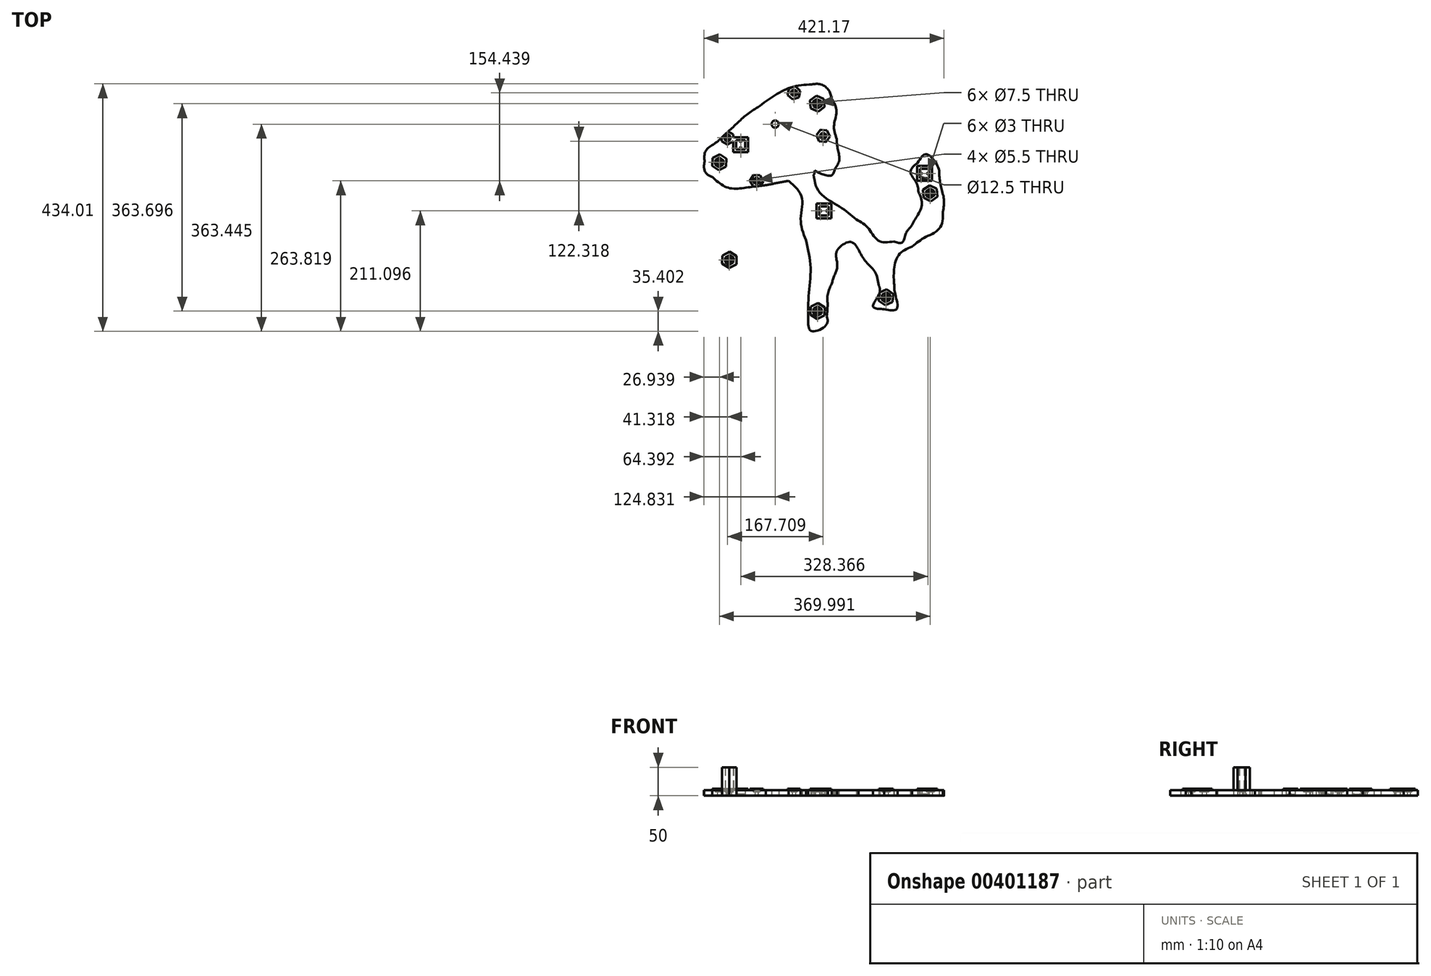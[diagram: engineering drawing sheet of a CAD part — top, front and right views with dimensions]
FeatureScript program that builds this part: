
annotation { "Feature Type Name" : "Feature", "Feature Type Description" : "" }
export const myFeature = defineFeature(function(context is Context, id is Id, definition is map)
    precondition{}
    {
        {
            var Q0;
            Q0=qCreatedBy(makeId("Top.planeOp"),FACE);
            var sketch = newSketch(context, id + "F0", { "sketchPlane" : qUnion([Q0])});
            skFitSpline(sketch, "E0", {"points": [v(-38.84, 161.13) * mm, v(-39.72, 129.92) * mm, v(-16.07, 104.3) * mm, v(-15.19, 73.39) * mm]});
            skFitSpline(sketch, "E1", {"points": [v(-15.19, 73.39) * mm, v(-15.53, 64.76) * mm, v(-18.42, 52.35) * mm, v(-28.63, 51.32) * mm]});
            skFitSpline(sketch, "E2", {"points": [v(-28.63, 51.32) * mm, v(-52.74, 44.98) * mm, v(-77.2, 39.98) * mm, v(-101.67, 35.25) * mm]});
            skFitSpline(sketch, "E3", {"points": [v(-101.67, 35.25) * mm, v(-133.26, 31.3) * mm, v(-168.43, 30.9) * mm, v(-195.67, 49.82) * mm]});
            skFitSpline(sketch, "E4", {"points": [v(-195.67, 49.82) * mm, v(-205.2, 54.88) * mm, v(-210.11, 65.3) * mm, v(-209.1, 75.9) * mm]});
            skFitSpline(sketch, "E5", {"points": [v(-209.1, 75.9) * mm, v(-207.12, 95.75) * mm, v(-190.25, 109.16) * mm, v(-176.41, 121.6) * mm]});
            skFitSpline(sketch, "E6", {"points": [v(-176.41, 121.6) * mm, v(-156.98, 139.28) * mm, v(-137.5, 157.08) * mm, v(-115.79, 172) * mm]});
            skFitSpline(sketch, "E7", {"points": [v(-115.79, 172) * mm, v(-87.6, 191.72) * mm, v(-55.7, 207.5) * mm, v(-21.28, 211.98) * mm]});
            skFitSpline(sketch, "E8", {"points": [v(-21.28, 211.98) * mm, v(-6.12, 212.25) * mm, v(8.26, 202.46) * mm, v(13.2, 188.07) * mm]});
            skFitSpline(sketch, "E9", {"points": [v(13.2, 188.07) * mm, v(22.3, 165.18) * mm, v(17.8, 140.05) * mm, v(22.57, 116.36) * mm]});
            skFitSpline(sketch, "E10", {"points": [v(22.57, 116.36) * mm, v(24.31, 98.94) * mm, v(27.2, 79.88) * mm, v(19.1, 63.6) * mm]});
            skFitSpline(sketch, "E11", {"points": [v(19.1, 63.6) * mm, v(13.05, 52.18) * mm, v(-8.03, 56.68) * mm, v(-17.41, 61.85) * mm]});
            skFitSpline(sketch, "E12", {"points": [v(-62.27, 43.42) * mm, v(-38.7, 13.78) * mm, v(-40.53, -25.96) * mm, v(-31.57, -60.94) * mm]});
            skFitSpline(sketch, "E13", {"points": [v(-31.57, -60.94) * mm, v(-23.4, -107.85) * mm, v(-26.4, -155.64) * mm, v(-27.47, -202.97) * mm]});
            skFitSpline(sketch, "E14", {"points": [v(-27.47, -202.97) * mm, v(-21.7, -220.56) * mm, v(4.44, -209.57) * mm, v(4.98, -194.23) * mm]});
            skFitSpline(sketch, "E15", {"points": [v(4.98, -194.23) * mm, v(6.6, -175.33) * mm, v(6.88, -156) * mm, v(13.8, -138) * mm]});
            skFitSpline(sketch, "E16", {"points": [v(13.8, -138) * mm, v(18.17, -124.09) * mm, v(23.35, -109.87) * mm, v(22.36, -95.12) * mm]});
            skFitSpline(sketch, "E17", {"points": [v(22.36, -95.12) * mm, v(24.1, -78.11) * mm, v(46.94, -64.43) * mm, v(60.72, -77.63) * mm]});
            skFitSpline(sketch, "E18", {"points": [v(60.72, -77.63) * mm, v(73.1, -98.24) * mm, v(89.77, -117.1) * mm, v(96.44, -140.58) * mm]});
            skFitSpline(sketch, "E19", {"points": [v(96.44, -140.58) * mm, v(97.66, -154.1) * mm, v(86.5, -177.33) * mm, v(105.7, -182.18) * mm]});
            skFitSpline(sketch, "E20", {"points": [v(105.7, -182.18) * mm, v(127.95, -181.8) * mm, v(125.17, -155.57) * mm, v(123.38, -140.16) * mm]});
            skFitSpline(sketch, "E21", {"points": [v(123.38, -140.16) * mm, v(123.03, -114.52) * mm, v(132.05, -86.5) * mm, v(155.03, -72.56) * mm]});
            skFitSpline(sketch, "E22", {"points": [v(155.03, -72.56) * mm, v(176.86, -56.73) * mm, v(203.36, -40.1) * mm, v(208.8, -11.55) * mm]});
            skFitSpline(sketch, "E23", {"points": [v(208.8, -11.55) * mm, v(210.76, 9.7) * mm, v(205.9, 30.86) * mm, v(202.52, 51.71) * mm]});
            skFitSpline(sketch, "E24", {"points": [v(202.52, 51.71) * mm, v(200.1, 68.08) * mm, v(179.66, 89.32) * mm, v(164.14, 73.98) * mm]});
            skFitSpline(sketch, "E25", {"points": [v(164.14, 73.98) * mm, v(151.98, 58.6) * mm, v(162.31, 39.48) * mm, v(166.07, 23) * mm]});
            skFitSpline(sketch, "E26", {"points": [v(166.07, 23) * mm, v(172.1, 1.47) * mm, v(162.48, -20.58) * mm, v(151.87, -39) * mm]});
            skFitSpline(sketch, "E27", {"points": [v(151.87, -39) * mm, v(144.15, -48.83) * mm, v(137.7, -65.26) * mm, v(122.78, -63.45) * mm]});
            skFitSpline(sketch, "E28", {"points": [v(122.78, -63.45) * mm, v(95.86, -62.15) * mm, v(77.57, -39.7) * mm, v(57.01, -25.17) * mm]});
            skFitSpline(sketch, "E29", {"points": [v(57.01, -25.17) * mm, v(28.57, -3) * mm, v(-8.3, 23.74) * mm, v(-18.27, 59.99) * mm]});
            skCircle(sketch, "E30", {"center": v(-85.42, 142.37) * mm, "radius": 6.25 * mm});
            skLineSegment(sketch, "E31", {"start": v(13.2, 188.07) * mm, "end": v(-41.55, 177.08) * mm});
            skLineSegment(sketch, "E32", {"start": v(-41.55, 177.08) * mm, "end": v(-38.84, 161.13) * mm});
            skLineSegment(sketch, "E33.bottom", {"start": v(-137.86, 98.34) * mm, "end": v(-153.86, 98.34) * mm});
            skLineSegment(sketch, "E33.top", {"start": v(-137.86, 114.34) * mm, "end": v(-153.86, 114.34) * mm});
            skLineSegment(sketch, "E33.left", {"start": v(-137.86, 98.34) * mm, "end": v(-137.86, 114.34) * mm});
            skLineSegment(sketch, "E33.right", {"start": v(-153.86, 98.34) * mm, "end": v(-153.86, 114.34) * mm});
            skPoint(sketch, "E33.middle", {"position": v(-145.86, 106.34) * mm});
            skLineSegment(sketch, "E34.bottom", {"start": v(8, -17.97) * mm, "end": v(-8, -17.97) * mm});
            skLineSegment(sketch, "E34.top", {"start": v(8, -1.97) * mm, "end": v(-8, -1.97) * mm});
            skLineSegment(sketch, "E34.left", {"start": v(8, -17.97) * mm, "end": v(8, -1.97) * mm});
            skLineSegment(sketch, "E34.right", {"start": v(-8, -17.97) * mm, "end": v(-8, -1.97) * mm});
            skPoint(sketch, "E34.middle", {"position": v(0, -9.97) * mm});
            skLineSegment(sketch, "E35.bottom", {"start": v(184.5, 47.75) * mm, "end": v(168.5, 47.75) * mm});
            skLineSegment(sketch, "E35.top", {"start": v(184.5, 63.75) * mm, "end": v(168.5, 63.75) * mm});
            skLineSegment(sketch, "E35.left", {"start": v(184.5, 47.75) * mm, "end": v(184.5, 63.75) * mm});
            skLineSegment(sketch, "E35.right", {"start": v(168.5, 47.75) * mm, "end": v(168.5, 63.75) * mm});
            skPoint(sketch, "E35.middle", {"position": v(176.5, 55.75) * mm});
            skLineSegment(sketch, "E36", {"start": v(0, 0) * mm, "end": v(0, 42.83) * mm, "construction": true});
            skLineSegment(sketch, "E37", {"start": v(-8, -1.97) * mm, "end": v(8, -17.97) * mm, "construction": true});
            skLineSegment(sketch, "E38", {"start": v(-294.78, 191.16) * mm, "end": v(0, -244.68) * mm, "construction": true});
            skLineSegment(sketch, "E39", {"start": v(279.03, -55.96) * mm, "end": v(24.58, 320.25) * mm, "construction": true});
            skLineSegment(sketch, "E40", {"start": v(285.1, -64.94) * mm, "end": v(20.46, -243.94) * mm, "construction": true});
            skLineSegment(sketch, "E41", {"start": v(92.7, 313.06) * mm, "end": v(-291.27, 53.36) * mm, "construction": true});
            skLineSegment(sketch, "E42", {"start": v(-168.93, 118.33) * mm, "end": v(-52.34, 197.19) * mm, "construction": true});
            skLineSegment(sketch, "E43", {"start": v(-52.34, 197.19) * mm, "end": v(-1.22, 121.6) * mm, "construction": true});
            skLineSegment(sketch, "E44", {"start": v(-1.22, 121.6) * mm, "end": v(-117.81, 42.75) * mm, "construction": true});
            skLineSegment(sketch, "E45", {"start": v(-117.81, 42.75) * mm, "end": v(-168.93, 118.33) * mm, "construction": true});
            skCircle(sketch, "E46", {"center": v(-117.81, 42.75) * mm, "radius": 2.75 * mm});
            skCircle(sketch, "E47.cCircle", {"center": v(-117.81, 42.75) * mm, "radius": 5.13 * mm, "construction": true});
            skLineSegment(sketch, "E47.0", {"start": v(-111.9, 42.69) * mm, "end": v(-114.9, 37.6) * mm});
            skLineSegment(sketch, "E47.1", {"start": v(-114.9, 37.6) * mm, "end": v(-120.82, 37.66) * mm});
            skLineSegment(sketch, "E47.2", {"start": v(-120.82, 37.66) * mm, "end": v(-123.73, 42.81) * mm});
            skLineSegment(sketch, "E47.3", {"start": v(-123.73, 42.81) * mm, "end": v(-120.71, 47.9) * mm});
            skLineSegment(sketch, "E47.4", {"start": v(-120.71, 47.9) * mm, "end": v(-114.8, 47.84) * mm});
            skLineSegment(sketch, "E47.5", {"start": v(-114.8, 47.84) * mm, "end": v(-111.9, 42.69) * mm});
            skPoint(sketch, "E47.0.midPoint", {"position": v(-113.4, 40.14) * mm});
            skCircle(sketch, "E48.cCircle", {"center": v(-117.81, 42.75) * mm, "radius": 10.12 * mm, "construction": true});
            skLineSegment(sketch, "E48.0", {"start": v(-106.12, 42.62) * mm, "end": v(-112.07, 32.56) * mm});
            skLineSegment(sketch, "E48.1", {"start": v(-112.07, 32.56) * mm, "end": v(-123.76, 32.69) * mm});
            skLineSegment(sketch, "E48.2", {"start": v(-123.76, 32.69) * mm, "end": v(-129.5, 42.87) * mm});
            skLineSegment(sketch, "E48.3", {"start": v(-129.5, 42.87) * mm, "end": v(-123.55, 52.94) * mm});
            skLineSegment(sketch, "E48.4", {"start": v(-123.55, 52.94) * mm, "end": v(-111.86, 52.81) * mm});
            skLineSegment(sketch, "E48.5", {"start": v(-111.86, 52.81) * mm, "end": v(-106.12, 42.62) * mm});
            skPoint(sketch, "E48.0.midPoint", {"position": v(-109.1, 37.6) * mm});
            skCircle(sketch, "E49", {"center": v(-168.93, 118.33) * mm, "radius": 2.75 * mm});
            skCircle(sketch, "E50.cCircle", {"center": v(-168.93, 118.33) * mm, "radius": 5.13 * mm, "construction": true});
            skLineSegment(sketch, "E50.0", {"start": v(-168.93, 112.42) * mm, "end": v(-174.06, 115.37) * mm});
            skLineSegment(sketch, "E50.1", {"start": v(-174.06, 115.37) * mm, "end": v(-174.06, 121.3) * mm});
            skLineSegment(sketch, "E50.2", {"start": v(-174.06, 121.3) * mm, "end": v(-168.93, 124.25) * mm});
            skLineSegment(sketch, "E50.3", {"start": v(-168.93, 124.25) * mm, "end": v(-163.8, 121.3) * mm});
            skLineSegment(sketch, "E50.4", {"start": v(-163.8, 121.3) * mm, "end": v(-163.8, 115.37) * mm});
            skLineSegment(sketch, "E50.5", {"start": v(-163.8, 115.37) * mm, "end": v(-168.93, 112.42) * mm});
            skPoint(sketch, "E50.0.midPoint", {"position": v(-171.5, 113.9) * mm});
            skCircle(sketch, "E51.cCircle", {"center": v(-168.93, 118.33) * mm, "radius": 10.12 * mm, "construction": true});
            skLineSegment(sketch, "E51.0", {"start": v(-158.8, 112.49) * mm, "end": v(-168.93, 106.64) * mm});
            skLineSegment(sketch, "E51.1", {"start": v(-168.93, 106.64) * mm, "end": v(-179.06, 112.49) * mm});
            skLineSegment(sketch, "E51.2", {"start": v(-179.06, 112.49) * mm, "end": v(-179.06, 124.18) * mm});
            skLineSegment(sketch, "E51.3", {"start": v(-179.06, 124.18) * mm, "end": v(-168.93, 130.03) * mm});
            skLineSegment(sketch, "E51.4", {"start": v(-168.93, 130.03) * mm, "end": v(-158.8, 124.18) * mm});
            skLineSegment(sketch, "E51.5", {"start": v(-158.8, 124.18) * mm, "end": v(-158.8, 112.49) * mm});
            skPoint(sketch, "E51.0.midPoint", {"position": v(-163.87, 109.57) * mm});
            skLineSegment(sketch, "E52.bottom", {"start": v(-132.86, 93.34) * mm, "end": v(-158.86, 93.34) * mm});
            skLineSegment(sketch, "E52.top", {"start": v(-132.86, 119.34) * mm, "end": v(-158.86, 119.34) * mm});
            skLineSegment(sketch, "E52.left", {"start": v(-132.86, 93.34) * mm, "end": v(-132.86, 119.34) * mm});
            skLineSegment(sketch, "E52.right", {"start": v(-158.86, 93.34) * mm, "end": v(-158.86, 119.34) * mm});
            skLineSegment(sketch, "E53.bottom", {"start": v(13, -22.97) * mm, "end": v(-13, -22.97) * mm});
            skLineSegment(sketch, "E53.top", {"start": v(13, 3.03) * mm, "end": v(-13, 3.03) * mm});
            skLineSegment(sketch, "E53.left", {"start": v(13, -22.97) * mm, "end": v(13, 3.03) * mm});
            skLineSegment(sketch, "E53.right", {"start": v(-13, -22.97) * mm, "end": v(-13, 3.03) * mm});
            skLineSegment(sketch, "E54.bottom", {"start": v(189.5, 42.75) * mm, "end": v(163.5, 42.75) * mm});
            skLineSegment(sketch, "E54.top", {"start": v(189.5, 68.75) * mm, "end": v(163.5, 68.75) * mm});
            skLineSegment(sketch, "E54.left", {"start": v(189.5, 42.75) * mm, "end": v(189.5, 68.75) * mm});
            skLineSegment(sketch, "E54.right", {"start": v(163.5, 42.75) * mm, "end": v(163.5, 68.75) * mm});
            skCircle(sketch, "E55", {"center": v(-1.22, 121.6) * mm, "radius": 2.75 * mm});
            skCircle(sketch, "E56", {"center": v(-52.34, 197.19) * mm, "radius": 2.75 * mm});
            skCircle(sketch, "E57.cCircle", {"center": v(-1.22, 121.6) * mm, "radius": 5.12 * mm, "construction": true});
            skLineSegment(sketch, "E57.0", {"start": v(4.66, 120.98) * mm, "end": v(1.18, 116.2) * mm});
            skLineSegment(sketch, "E57.1", {"start": v(1.18, 116.2) * mm, "end": v(-4.7, 116.82) * mm});
            skLineSegment(sketch, "E57.2", {"start": v(-4.7, 116.82) * mm, "end": v(-7.1, 122.23) * mm});
            skLineSegment(sketch, "E57.3", {"start": v(-7.1, 122.23) * mm, "end": v(-3.62, 127.01) * mm});
            skLineSegment(sketch, "E57.4", {"start": v(-3.62, 127.01) * mm, "end": v(2.26, 126.39) * mm});
            skLineSegment(sketch, "E57.5", {"start": v(2.26, 126.39) * mm, "end": v(4.66, 120.98) * mm});
            skPoint(sketch, "E57.0.midPoint", {"position": v(2.92, 118.59) * mm});
            skCircle(sketch, "E58.cCircle", {"center": v(-52.34, 197.19) * mm, "radius": 5.13 * mm, "construction": true});
            skLineSegment(sketch, "E58.0", {"start": v(-47.98, 193.2) * mm, "end": v(-53.62, 191.4) * mm});
            skLineSegment(sketch, "E58.1", {"start": v(-53.62, 191.4) * mm, "end": v(-57.99, 195.4) * mm});
            skLineSegment(sketch, "E58.2", {"start": v(-57.99, 195.4) * mm, "end": v(-56.7, 201.18) * mm});
            skLineSegment(sketch, "E58.3", {"start": v(-56.7, 201.18) * mm, "end": v(-51.07, 202.97) * mm});
            skLineSegment(sketch, "E58.4", {"start": v(-51.07, 202.97) * mm, "end": v(-46.7, 198.97) * mm});
            skLineSegment(sketch, "E58.5", {"start": v(-46.7, 198.97) * mm, "end": v(-47.98, 193.2) * mm});
            skPoint(sketch, "E58.0.midPoint", {"position": v(-50.8, 192.3) * mm});
            skCircle(sketch, "E59.cCircle", {"center": v(-1.22, 121.6) * mm, "radius": 10.12 * mm, "construction": true});
            skLineSegment(sketch, "E59.0", {"start": v(10.4, 120.37) * mm, "end": v(3.52, 110.92) * mm});
            skLineSegment(sketch, "E59.1", {"start": v(3.52, 110.92) * mm, "end": v(-8.1, 112.15) * mm});
            skLineSegment(sketch, "E59.2", {"start": v(-8.1, 112.15) * mm, "end": v(-12.85, 122.84) * mm});
            skLineSegment(sketch, "E59.3", {"start": v(-12.85, 122.84) * mm, "end": v(-5.97, 132.29) * mm});
            skLineSegment(sketch, "E59.4", {"start": v(-5.97, 132.29) * mm, "end": v(5.66, 131.05) * mm});
            skLineSegment(sketch, "E59.5", {"start": v(5.66, 131.05) * mm, "end": v(10.4, 120.37) * mm});
            skPoint(sketch, "E59.0.midPoint", {"position": v(6.96, 115.64) * mm});
            skCircle(sketch, "E60.cCircle", {"center": v(-52.34, 197.19) * mm, "radius": 10.12 * mm, "construction": true});
            skLineSegment(sketch, "E60.0", {"start": v(-54.87, 185.77) * mm, "end": v(-63.5, 193.67) * mm});
            skLineSegment(sketch, "E60.1", {"start": v(-63.5, 193.67) * mm, "end": v(-60.97, 205.08) * mm});
            skLineSegment(sketch, "E60.2", {"start": v(-60.97, 205.08) * mm, "end": v(-49.82, 208.6) * mm});
            skLineSegment(sketch, "E60.3", {"start": v(-49.82, 208.6) * mm, "end": v(-41.2, 200.7) * mm});
            skLineSegment(sketch, "E60.4", {"start": v(-41.2, 200.7) * mm, "end": v(-43.72, 189.3) * mm});
            skLineSegment(sketch, "E60.5", {"start": v(-43.72, 189.3) * mm, "end": v(-54.87, 185.77) * mm});
            skPoint(sketch, "E60.0.midPoint", {"position": v(-59.18, 189.72) * mm});
            skCircle(sketch, "E61", {"center": v(-183.31, 75.26) * mm, "radius": 3.75 * mm});
            skCircle(sketch, "E62", {"center": v(-11.46, 178.03) * mm, "radius": 3.75 * mm});
            skCircle(sketch, "E63", {"center": v(-10.96, -185.67) * mm, "radius": 3.75 * mm});
            skCircle(sketch, "E64", {"center": v(109.1, -161.5) * mm, "radius": 3.75 * mm});
            skCircle(sketch, "E65", {"center": v(186.68, 20.92) * mm, "radius": 3.75 * mm});
            skCircle(sketch, "E66.cCircle", {"center": v(-10.96, -185.67) * mm, "radius": 7.12 * mm, "construction": true});
            skLineSegment(sketch, "E66.0", {"start": v(-4.02, -190.1) * mm, "end": v(-11.32, -193.89) * mm});
            skLineSegment(sketch, "E66.1", {"start": v(-11.32, -193.89) * mm, "end": v(-18.26, -189.46) * mm});
            skLineSegment(sketch, "E66.2", {"start": v(-18.26, -189.46) * mm, "end": v(-17.9, -181.24) * mm});
            skLineSegment(sketch, "E66.3", {"start": v(-17.9, -181.24) * mm, "end": v(-10.6, -177.45) * mm});
            skLineSegment(sketch, "E66.4", {"start": v(-10.6, -177.45) * mm, "end": v(-3.66, -181.87) * mm});
            skLineSegment(sketch, "E66.5", {"start": v(-3.66, -181.87) * mm, "end": v(-4.02, -190.1) * mm});
            skPoint(sketch, "E66.0.midPoint", {"position": v(-7.67, -191.99) * mm});
            skCircle(sketch, "E67.cCircle", {"center": v(-10.96, -185.67) * mm, "radius": 12.12 * mm, "construction": true});
            skLineSegment(sketch, "E67.0", {"start": v(0.84, -193.2) * mm, "end": v(-11.58, -199.65) * mm});
            skLineSegment(sketch, "E67.1", {"start": v(-11.58, -199.65) * mm, "end": v(-23.38, -192.13) * mm});
            skLineSegment(sketch, "E67.2", {"start": v(-23.38, -192.13) * mm, "end": v(-22.77, -178.14) * mm});
            skLineSegment(sketch, "E67.3", {"start": v(-22.77, -178.14) * mm, "end": v(-10.34, -171.68) * mm});
            skLineSegment(sketch, "E67.4", {"start": v(-10.34, -171.68) * mm, "end": v(1.46, -179.2) * mm});
            skLineSegment(sketch, "E67.5", {"start": v(1.46, -179.2) * mm, "end": v(0.84, -193.2) * mm});
            skPoint(sketch, "E67.0.midPoint", {"position": v(-5.37, -196.43) * mm});
            skCircle(sketch, "E68.cCircle", {"center": v(109.1, -161.5) * mm, "radius": 7.12 * mm, "construction": true});
            skLineSegment(sketch, "E68.0", {"start": v(115.9, -166.13) * mm, "end": v(108.5, -169.71) * mm});
            skLineSegment(sketch, "E68.1", {"start": v(108.5, -169.71) * mm, "end": v(101.7, -165.08) * mm});
            skLineSegment(sketch, "E68.2", {"start": v(101.7, -165.08) * mm, "end": v(102.3, -156.88) * mm});
            skLineSegment(sketch, "E68.3", {"start": v(102.3, -156.88) * mm, "end": v(109.71, -153.3) * mm});
            skLineSegment(sketch, "E68.4", {"start": v(109.71, -153.3) * mm, "end": v(116.52, -157.93) * mm});
            skLineSegment(sketch, "E68.5", {"start": v(116.52, -157.93) * mm, "end": v(115.9, -166.13) * mm});
            skPoint(sketch, "E68.0.midPoint", {"position": v(112.2, -167.92) * mm});
            skCircle(sketch, "E69.cCircle", {"center": v(109.1, -161.5) * mm, "radius": 12.12 * mm, "construction": true});
            skLineSegment(sketch, "E69.0", {"start": v(96.5, -167.6) * mm, "end": v(97.53, -153.63) * mm});
            skLineSegment(sketch, "E69.1", {"start": v(97.53, -153.63) * mm, "end": v(110.14, -147.54) * mm});
            skLineSegment(sketch, "E69.2", {"start": v(110.14, -147.54) * mm, "end": v(121.71, -155.42) * mm});
            skLineSegment(sketch, "E69.3", {"start": v(121.71, -155.42) * mm, "end": v(120.68, -169.38) * mm});
            skLineSegment(sketch, "E69.4", {"start": v(120.68, -169.38) * mm, "end": v(108.07, -175.47) * mm});
            skLineSegment(sketch, "E69.5", {"start": v(108.07, -175.47) * mm, "end": v(96.5, -167.6) * mm});
            skPoint(sketch, "E69.0.midPoint", {"position": v(97.01, -160.61) * mm});
            skCircle(sketch, "E70.cCircle", {"center": v(186.68, 20.92) * mm, "radius": 7.12 * mm, "construction": true});
            skLineSegment(sketch, "E70.0", {"start": v(194.08, 17.32) * mm, "end": v(187.26, 12.7) * mm});
            skLineSegment(sketch, "E70.1", {"start": v(187.26, 12.7) * mm, "end": v(179.87, 16.3) * mm});
            skLineSegment(sketch, "E70.2", {"start": v(179.87, 16.3) * mm, "end": v(179.28, 24.51) * mm});
            skLineSegment(sketch, "E70.3", {"start": v(179.28, 24.51) * mm, "end": v(186.1, 29.12) * mm});
            skLineSegment(sketch, "E70.4", {"start": v(186.1, 29.12) * mm, "end": v(193.5, 25.53) * mm});
            skLineSegment(sketch, "E70.5", {"start": v(193.5, 25.53) * mm, "end": v(194.08, 17.32) * mm});
            skPoint(sketch, "E70.0.midPoint", {"position": v(190.67, 15.01) * mm});
            skCircle(sketch, "E71.cCircle", {"center": v(186.68, 20.92) * mm, "radius": 12.12 * mm, "construction": true});
            skLineSegment(sketch, "E71.0", {"start": v(199.27, 14.8) * mm, "end": v(187.67, 6.95) * mm});
            skLineSegment(sketch, "E71.1", {"start": v(187.67, 6.95) * mm, "end": v(175.08, 13.07) * mm});
            skLineSegment(sketch, "E71.2", {"start": v(175.08, 13.07) * mm, "end": v(174.09, 27.04) * mm});
            skLineSegment(sketch, "E71.3", {"start": v(174.09, 27.04) * mm, "end": v(185.69, 34.88) * mm});
            skLineSegment(sketch, "E71.4", {"start": v(185.69, 34.88) * mm, "end": v(198.28, 28.76) * mm});
            skLineSegment(sketch, "E71.5", {"start": v(198.28, 28.76) * mm, "end": v(199.27, 14.8) * mm});
            skPoint(sketch, "E71.0.midPoint", {"position": v(193.47, 10.87) * mm});
            skCircle(sketch, "E72.cCircle", {"center": v(-183.31, 75.26) * mm, "radius": 7.12 * mm, "construction": true});
            skLineSegment(sketch, "E72.0", {"start": v(-176.47, 70.7) * mm, "end": v(-183.84, 67.05) * mm});
            skLineSegment(sketch, "E72.1", {"start": v(-183.84, 67.05) * mm, "end": v(-190.69, 71.62) * mm});
            skLineSegment(sketch, "E72.2", {"start": v(-190.69, 71.62) * mm, "end": v(-190.16, 79.83) * mm});
            skLineSegment(sketch, "E72.3", {"start": v(-190.16, 79.83) * mm, "end": v(-182.78, 83.47) * mm});
            skLineSegment(sketch, "E72.4", {"start": v(-182.78, 83.47) * mm, "end": v(-175.94, 78.9) * mm});
            skLineSegment(sketch, "E72.5", {"start": v(-175.94, 78.9) * mm, "end": v(-176.47, 70.7) * mm});
            skPoint(sketch, "E72.0.midPoint", {"position": v(-180.15, 68.87) * mm});
            skCircle(sketch, "E73.cCircle", {"center": v(-183.31, 75.26) * mm, "radius": 12.12 * mm, "construction": true});
            skLineSegment(sketch, "E73.0", {"start": v(-171.66, 67.5) * mm, "end": v(-184.21, 61.29) * mm});
            skLineSegment(sketch, "E73.1", {"start": v(-184.21, 61.29) * mm, "end": v(-195.86, 69.06) * mm});
            skLineSegment(sketch, "E73.2", {"start": v(-195.86, 69.06) * mm, "end": v(-194.96, 83.03) * mm});
            skLineSegment(sketch, "E73.3", {"start": v(-194.96, 83.03) * mm, "end": v(-182.4, 89.23) * mm});
            skLineSegment(sketch, "E73.4", {"start": v(-182.4, 89.23) * mm, "end": v(-170.76, 81.47) * mm});
            skLineSegment(sketch, "E73.5", {"start": v(-170.76, 81.47) * mm, "end": v(-171.66, 67.5) * mm});
            skPoint(sketch, "E73.0.midPoint", {"position": v(-177.94, 64.4) * mm});
            skCircle(sketch, "E74.cCircle", {"center": v(-11.46, 178.03) * mm, "radius": 7.12 * mm, "construction": true});
            skLineSegment(sketch, "E74.0", {"start": v(-3.94, 174.7) * mm, "end": v(-10.59, 169.85) * mm});
            skLineSegment(sketch, "E74.1", {"start": v(-10.59, 169.85) * mm, "end": v(-18.1, 173.18) * mm});
            skLineSegment(sketch, "E74.2", {"start": v(-18.1, 173.18) * mm, "end": v(-18.99, 181.36) * mm});
            skLineSegment(sketch, "E74.3", {"start": v(-18.99, 181.36) * mm, "end": v(-12.34, 186.2) * mm});
            skLineSegment(sketch, "E74.4", {"start": v(-12.34, 186.2) * mm, "end": v(-4.82, 182.88) * mm});
            skLineSegment(sketch, "E74.5", {"start": v(-4.82, 182.88) * mm, "end": v(-3.94, 174.7) * mm});
            skPoint(sketch, "E74.0.midPoint", {"position": v(-7.26, 172.27) * mm});
            skCircle(sketch, "E75.cCircle", {"center": v(-11.46, 178.03) * mm, "radius": 12.12 * mm, "construction": true});
            skLineSegment(sketch, "E75.0", {"start": v(1.34, 172.36) * mm, "end": v(-9.97, 164.1) * mm});
            skLineSegment(sketch, "E75.1", {"start": v(-9.97, 164.1) * mm, "end": v(-22.77, 169.77) * mm});
            skLineSegment(sketch, "E75.2", {"start": v(-22.77, 169.77) * mm, "end": v(-24.27, 183.7) * mm});
            skLineSegment(sketch, "E75.3", {"start": v(-24.27, 183.7) * mm, "end": v(-12.96, 191.95) * mm});
            skLineSegment(sketch, "E75.4", {"start": v(-12.96, 191.95) * mm, "end": v(-0.16, 186.28) * mm});
            skLineSegment(sketch, "E75.5", {"start": v(-0.16, 186.28) * mm, "end": v(1.34, 172.36) * mm});
            skPoint(sketch, "E75.0.midPoint", {"position": v(-4.32, 168.24) * mm});
            skLineSegment(sketch, "E76", {"start": v(-8, -9.97) * mm, "end": v(8, -9.97) * mm, "construction": true});
            skCircle(sketch, "E77", {"center": v(-6, -9.97) * mm, "radius": 1.5 * mm});
            skCircle(sketch, "E78", {"center": v(6, -9.97) * mm, "radius": 1.5 * mm});
            skLineSegment(sketch, "E79", {"start": v(-145.86, 98.34) * mm, "end": v(-145.86, 114.34) * mm, "construction": true});
            skCircle(sketch, "E80", {"center": v(-145.86, 100.34) * mm, "radius": 1.5 * mm});
            skCircle(sketch, "E81", {"center": v(-145.86, 112.34) * mm, "radius": 1.5 * mm});
            skLineSegment(sketch, "E82", {"start": v(168.5, 55.75) * mm, "end": v(184.5, 55.75) * mm, "construction": true});
            skCircle(sketch, "E83", {"center": v(170.5, 55.75) * mm, "radius": 1.5 * mm});
            skCircle(sketch, "E84", {"center": v(182.5, 55.75) * mm, "radius": 1.5 * mm});
            skSolve(sketch);
        }
        {
            var Q0;
            {var subQ5=sQuery(id+"F0.wireOp",EDGE,"E0");Q0=makeQuery(id+"F0.imprint","IMPRINT",FACE,{"disambiguationData":[TD([[makeQuery(id+"F0.imprint","IMPRINT",EDGE,{"derivedFrom":subQ5}),-1.0]])]});}
            var Q1;
            {var subQ7=sQuery(id+"F0.wireOp",EDGE,"E13");Q1=makeQuery(id+"F0.imprint","IMPRINT",FACE,{"disambiguationData":[TD([[makeQuery(id+"F0.imprint","IMPRINT",EDGE,{"derivedFrom":subQ7}),1.0]])]});}
            var Q2;
            {var subQ2=sQuery(id+"F0.wireOp",EDGE,"E0");Q2=makeQuery(id+"F0.imprint","IMPRINT",FACE,{"disambiguationData":[TD([[makeQuery(id+"F0.imprint","IMPRINT",EDGE,{"derivedFrom":subQ2}),1.0]])]});}
            extrude(context, id + "F1", {"entities" : qUnion([Q0, Q1, Q2]), "depth" : 10 * mm});
        }
        {
            var Q0;
            Q0=makeQuery(id+"F0.imprint","IMPRINT",FACE,{"disambiguationData":[TD([[makeQuery(id+"F0.imprint","IMPRINT",EDGE,{"derivedFrom":sQuery(id+"F0.wireOp",EDGE,"E61")}),-1.0]])]});
            var Q1;
            Q1=makeQuery(id+"F0.imprint","IMPRINT",FACE,{"disambiguationData":[TD([[makeQuery(id+"F0.imprint","IMPRINT",EDGE,{"derivedFrom":sQuery(id+"F0.wireOp",EDGE,"E46")}),-1.0]])]});
            var Q2;
            Q2=makeQuery(id+"F0.imprint","IMPRINT",FACE,{"disambiguationData":[TD([[makeQuery(id+"F0.imprint","IMPRINT",EDGE,{"derivedFrom":sQuery(id+"F0.wireOp",EDGE,"E49")}),-1.0]])]});
            var Q3;
            Q3=makeQuery(id+"F0.imprint","IMPRINT",FACE,{"disambiguationData":[TD([[makeQuery(id+"F0.imprint","IMPRINT",EDGE,{"derivedFrom":sQuery(id+"F0.wireOp",EDGE,"E56")}),-1.0]])]});
            var Q4;
            Q4=makeQuery(id+"F0.imprint","IMPRINT",FACE,{"disambiguationData":[TD([[makeQuery(id+"F0.imprint","IMPRINT",EDGE,{"derivedFrom":sQuery(id+"F0.wireOp",EDGE,"E62")}),-1.0]])]});
            var Q5;
            Q5=makeQuery(id+"F0.imprint","IMPRINT",FACE,{"disambiguationData":[TD([[makeQuery(id+"F0.imprint","IMPRINT",EDGE,{"derivedFrom":sQuery(id+"F0.wireOp",EDGE,"E55")}),-1.0]])]});
            var Q6;
            Q6=makeQuery(id+"F0.imprint","IMPRINT",FACE,{"disambiguationData":[TD([[makeQuery(id+"F0.imprint","IMPRINT",EDGE,{"derivedFrom":sQuery(id+"F0.wireOp",EDGE,"E63")}),-1.0]])]});
            var Q7;
            Q7=makeQuery(id+"F0.imprint","IMPRINT",FACE,{"disambiguationData":[TD([[makeQuery(id+"F0.imprint","IMPRINT",EDGE,{"derivedFrom":sQuery(id+"F0.wireOp",EDGE,"E64")}),-1.0]])]});
            var Q8;
            Q8=makeQuery(id+"F0.imprint","IMPRINT",FACE,{"disambiguationData":[TD([[makeQuery(id+"F0.imprint","IMPRINT",EDGE,{"derivedFrom":sQuery(id+"F0.wireOp",EDGE,"E65")}),-1.0]])]});
            var Q9;
            {var subQ0=sQuery(id+"F0.wireOp",EDGE,"E74.4");var subQ1=sQuery(id+"F0.wireOp",EDGE,"E31");var subQ2=makeQuery(id+"F0.imprint","INTERSECT",VERTEX,{"derivedFrom":[subQ1,subQ0]});Q9=makeQuery(id+"F0.imprint","IMPRINT",FACE,{"disambiguationData":[TD([[makeQuery(id+"F0.imprint","IMPRINT",EDGE,{"disambiguationData":[TD([[subQ2,-1.0]])],"derivedFrom":subQ1}),-1.0]])]});}
            extrude(context, id + "F2", {"entities" : qUnion([Q0, Q1, Q2, Q3, Q4, Q5, Q6, Q7, Q8, Q9]), "depth" : 7.5 * mm});
        }
        {
            var Q0;
            Q0=makeQuery(id+"F0.imprint","IMPRINT",FACE,{"disambiguationData":[TD([[makeQuery(id+"F0.imprint","IMPRINT",EDGE,{"derivedFrom":sQuery(id+"F0.wireOp",EDGE,"E33.bottom")}),-1.0]])]});
            var Q1;
            Q1=makeQuery(id+"F0.imprint","IMPRINT",FACE,{"disambiguationData":[TD([[makeQuery(id+"F0.imprint","IMPRINT",EDGE,{"derivedFrom":sQuery(id+"F0.wireOp",EDGE,"E34.bottom")}),-1.0]])]});
            var Q2;
            Q2=makeQuery(id+"F0.imprint","IMPRINT",FACE,{"disambiguationData":[TD([[makeQuery(id+"F0.imprint","IMPRINT",EDGE,{"derivedFrom":sQuery(id+"F0.wireOp",EDGE,"E35.bottom")}),-1.0]])]});
            extrude(context, id + "F3", {"entities" : qUnion([Q0, Q1, Q2]), "depth" : 2.5 * mm});
        }
        {
            var Q0;
            Q0=makeQuery(id+"F0.imprint","IMPRINT",FACE,{"disambiguationData":[TD([[makeQuery(id+"F0.imprint","IMPRINT",EDGE,{"derivedFrom":sQuery(id+"F0.wireOp",EDGE,"E72.0")}),1.0]])]});
            var Q1;
            Q1=makeQuery(id+"F0.imprint","IMPRINT",FACE,{"disambiguationData":[TD([[makeQuery(id+"F0.imprint","IMPRINT",EDGE,{"derivedFrom":sQuery(id+"F0.wireOp",EDGE,"E50.0")}),1.0]])]});
            var Q2;
            Q2=makeQuery(id+"F0.imprint","IMPRINT",FACE,{"disambiguationData":[TD([[makeQuery(id+"F0.imprint","IMPRINT",EDGE,{"derivedFrom":sQuery(id+"F0.wireOp",EDGE,"E58.0")}),1.0]])]});
            var Q3;
            Q3=makeQuery(id+"F0.imprint","IMPRINT",FACE,{"disambiguationData":[TD([[makeQuery(id+"F0.imprint","IMPRINT",EDGE,{"derivedFrom":sQuery(id+"F0.wireOp",EDGE,"E74.0")}),1.0]])]});
            var Q4;
            Q4=makeQuery(id+"F0.imprint","IMPRINT",FACE,{"disambiguationData":[TD([[makeQuery(id+"F0.imprint","IMPRINT",EDGE,{"derivedFrom":sQuery(id+"F0.wireOp",EDGE,"E47.0")}),1.0]])]});
            var Q5;
            Q5=makeQuery(id+"F0.imprint","IMPRINT",FACE,{"disambiguationData":[TD([[makeQuery(id+"F0.imprint","IMPRINT",EDGE,{"derivedFrom":sQuery(id+"F0.wireOp",EDGE,"E57.0")}),1.0]])]});
            var Q6;
            {var subQ8=sQuery(id+"F0.wireOp",EDGE,"E75.3");Q6=makeQuery(id+"F0.imprint","IMPRINT",FACE,{"disambiguationData":[TD([[makeQuery(id+"F0.imprint","IMPRINT",EDGE,{"derivedFrom":subQ8}),-1.0]])]});}
            var Q7;
            Q7=makeQuery(id+"F0.imprint","IMPRINT",FACE,{"disambiguationData":[TD([[makeQuery(id+"F0.imprint","IMPRINT",EDGE,{"derivedFrom":sQuery(id+"F0.wireOp",EDGE,"E34.bottom")}),1.0]])]});
            var Q8;
            Q8=makeQuery(id+"F0.imprint","IMPRINT",FACE,{"disambiguationData":[TD([[makeQuery(id+"F0.imprint","IMPRINT",EDGE,{"derivedFrom":sQuery(id+"F0.wireOp",EDGE,"E35.bottom")}),1.0]])]});
            var Q9;
            Q9=makeQuery(id+"F0.imprint","IMPRINT",FACE,{"disambiguationData":[TD([[makeQuery(id+"F0.imprint","IMPRINT",EDGE,{"derivedFrom":sQuery(id+"F0.wireOp",EDGE,"E70.0")}),1.0]])]});
            var Q10;
            Q10=makeQuery(id+"F0.imprint","IMPRINT",FACE,{"disambiguationData":[TD([[makeQuery(id+"F0.imprint","IMPRINT",EDGE,{"derivedFrom":sQuery(id+"F0.wireOp",EDGE,"E68.0")}),1.0]])]});
            var Q11;
            Q11=makeQuery(id+"F0.imprint","IMPRINT",FACE,{"disambiguationData":[TD([[makeQuery(id+"F0.imprint","IMPRINT",EDGE,{"derivedFrom":sQuery(id+"F0.wireOp",EDGE,"E66.0")}),1.0]])]});
            extrude(context, id + "F4", {"entities" : qUnion([Q0, Q1, Q2, Q3, Q4, Q5, Q6, Q7, Q8, Q9, Q10, Q11]), "operationType" : NewBodyOperationType.ADD, "depth" : 12.5 * mm});
        }
        {
            var Q0;
            Q0=makeQuery(id+"F0.imprint","IMPRINT",FACE,{"disambiguationData":[TD([[makeQuery(id+"F0.imprint","IMPRINT",EDGE,{"derivedFrom":sQuery(id+"F0.wireOp",EDGE,"E33.bottom")}),1.0]])]});
            var Q1;
            {var subQ0=sQuery(id+"F0.wireOp",EDGE,"E51.5");var subQ1=sQuery(id+"F0.wireOp",EDGE,"E51.0");var subQ2=makeQuery(id+"F0.imprint","INTERSECT",VERTEX,{"derivedFrom":[subQ1,subQ0]});Q1=makeQuery(id+"F0.imprint","IMPRINT",FACE,{"disambiguationData":[TD([[makeQuery(id+"F0.imprint","IMPRINT",EDGE,{"disambiguationData":[TD([[subQ2,-1.0]])],"derivedFrom":subQ1}),-1.0]])]});}
            extrude(context, id + "F5", {"entities" : qUnion([Q0, Q1]), "operationType" : NewBodyOperationType.ADD, "depth" : 12.5 * mm});
        }
        {
            var Q0;
            Q0=qCreatedBy(makeId("Top.planeOp"),FACE);
            var sketch = newSketch(context, id + "F6", { "sketchPlane" : qUnion([Q0])});
            skCircle(sketch, "E85", {"center": v(-165.72, -95.83) * mm, "radius": 3.75 * mm});
            skCircle(sketch, "E86.cCircle", {"center": v(-165.72, -95.83) * mm, "radius": 7.13 * mm, "construction": true});
            skLineSegment(sketch, "E86.0", {"start": v(-165.98, -104.05) * mm, "end": v(-172.97, -99.7) * mm});
            skLineSegment(sketch, "E86.1", {"start": v(-172.97, -99.7) * mm, "end": v(-172.7, -91.48) * mm});
            skLineSegment(sketch, "E86.2", {"start": v(-172.7, -91.48) * mm, "end": v(-165.45, -87.6) * mm});
            skLineSegment(sketch, "E86.3", {"start": v(-165.45, -87.6) * mm, "end": v(-158.46, -91.95) * mm});
            skLineSegment(sketch, "E86.4", {"start": v(-158.46, -91.95) * mm, "end": v(-158.73, -100.17) * mm});
            skLineSegment(sketch, "E86.5", {"start": v(-158.73, -100.17) * mm, "end": v(-165.98, -104.05) * mm});
            skPoint(sketch, "E86.0.midPoint", {"position": v(-169.48, -101.88) * mm});
            skCircle(sketch, "E87.cCircle", {"center": v(-165.72, -95.83) * mm, "radius": 12.5 * mm, "construction": true});
            skLineSegment(sketch, "E87.0", {"start": v(-166.19, -110.25) * mm, "end": v(-178.45, -102.63) * mm});
            skLineSegment(sketch, "E87.1", {"start": v(-178.45, -102.63) * mm, "end": v(-177.98, -88.2) * mm});
            skLineSegment(sketch, "E87.2", {"start": v(-177.98, -88.2) * mm, "end": v(-165.25, -81.4) * mm});
            skLineSegment(sketch, "E87.3", {"start": v(-165.25, -81.4) * mm, "end": v(-152.99, -89.02) * mm});
            skLineSegment(sketch, "E87.4", {"start": v(-152.99, -89.02) * mm, "end": v(-153.46, -103.45) * mm});
            skLineSegment(sketch, "E87.5", {"start": v(-153.46, -103.45) * mm, "end": v(-166.19, -110.25) * mm});
            skPoint(sketch, "E87.0.midPoint", {"position": v(-172.32, -106.44) * mm});
            skSolve(sketch);
        }
        {
            var Q0;
            Q0=makeQuery(id+"F6.imprint","IMPRINT",FACE,{"disambiguationData":[TD([[makeQuery(id+"F6.imprint","IMPRINT",EDGE,{"derivedFrom":sQuery(id+"F6.wireOp",EDGE,"E85")}),-1.0]])]});
            extrude(context, id + "F7", {"entities" : qUnion([Q0]), "depth" : 7.5 * mm});
        }
        {
            var Q0;
            Q0=makeQuery(id+"F6.imprint","IMPRINT",FACE,{"disambiguationData":[TD([[makeQuery(id+"F6.imprint","IMPRINT",EDGE,{"derivedFrom":sQuery(id+"F6.wireOp",EDGE,"E86.0")}),1.0]])]});
            extrude(context, id + "F8", {"entities" : qUnion([Q0]), "operationType" : NewBodyOperationType.ADD, "depth" : 50 * mm});
        }
    });
